# Revit family: Legrand universal standard floor boxes EN
name_source: partatom
category: Installations électriques
units: mm (PartAtom-declared; Revit-internal decimal feet)

## family parameters
Conserver l'orientation des annotations = Non
Cote de connecteur circulaire = Utiliser le diamètre
Couper avec des vides une fois chargée = Non
Hôte = Face
Partagée = Non
Point de calcul de pièce = Non
Type d'élément = Normal

## types (9) — shared parameters
00 = Reservation boitier : 00
000000 = Accessoire : Aucun
01 = Reservation boitier : 01
02 = Reservation boitier : 02
088000 = Couvercle : 088000
088001 = Couvercle : 088001
088002 = Couvercle : 088002
088003 = Couvercle : 088003
088004 = Couvercle : 088004
088005 = Couvercle : 088005
088006 = Couvercle : 088006
088007 = Couvercle : 088007
088008 = Couvercle : 088008
088015 = Plaque finition : 088015
088016 = Plaque finition : 088016
088017 = Plaque finition : 088017
088026 = Accessoire : 088026
088027 = Accessoire : 088027
088028 = Accessoire : 088028
088045 = Plaque finition : 088045
088046 = Plaque finition : 088046
088047 = Plaque finition : 088047
088048 = Plaque finition : 088048
088049 = Plaque finition : 088049
088050 = Plaque finition : 088050
088080 = Boitier d'encastrement : 088080
088081 = Accessoire : 088081
088082 = Accessoire : 088082
088083 = Accessoire : 088083
088086 = Accessoire : 088086 + 088088
088086-2 = Accessoire : 088086 + (2x088088)
088090 = Boitier d'encastrement : 088090
088091 = Boitier d'encastrement : 088091
088092 = Boitier d'encastrement : 088092
26 = Reservation boitier : 26
27 = Reservation boitier : 27
28 = Reservation boitier : 28
80 = Reservation boitier : 80
90 = Reservation boitier : 90
91 = Reservation boitier : 91
92 = Reservation boitier : 92
Auto = Type of floor : Auto adjustable
Brass = Finish : Brass
Fabricant = LEGRAND
Inox = Finish : Stainless steel
Plastic = Finish : Grey RAL 7031
StdB125 = Type of floor : In-screed under 125 mm
StdB170 = Type of floor : In-screed above 125 mm and under 170 mm
StdB250 = Type of floor : In-screed above 170 mm and under 250 mm
StdT = Type of floor : Raised floor
zero-valued in all types: Elévation par défaut

## per-type parameters (varying)
| type | Description | Frames | Support | Support appareillage |
| 8 modules 2x4 | Universal standard floor box 8 modules vertical | 088023 | 23 | Support appareillage : 088023 |
| 12 modules 2x6 | Universal standard floor box 12 modules vertical | 088024 | 24 | Support appareillage : 088024 |
| 16 modules 2x8 | Universal standard floor box 16 modules vertical | 088025 | 25 | Support appareillage : 088025 |
| 12 modules 3x4 | Universal standard floor box 12 modules horizontal adjustable | 088020 | 20 | Support appareillage : 088020 |
| 18 modules 3x6 | Universal standard floor box 18 modules horizontal adjustable | 088021 | 21 | Support appareillage : 088021 |
| 24 modules 3x8 | Universal standard floor box 24 modules horizontal adjustable | 088022 | 22 | Support appareillage : 088022 |
| Open frame 8-12 modules | Access unit standard lid 8/12 modules | 088039 | 39 | Support appareillage : 088039 |
| Open frame 12-18 modules | Access unit standard lid 12/18 modules | 088040 | 40 | Support appareillage : 088040 |
| Open frame 16-24 modules | Access unit standard lid 16/24 modules | 088041 | 41 | Support appareillage : 088041 |
